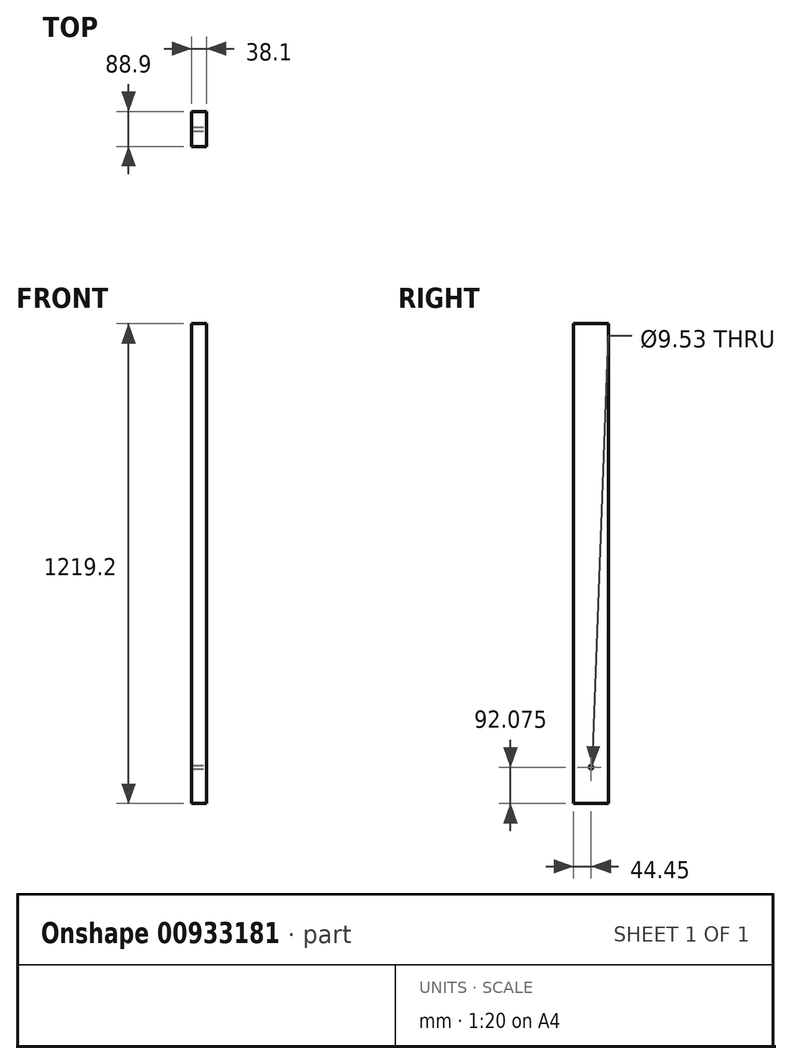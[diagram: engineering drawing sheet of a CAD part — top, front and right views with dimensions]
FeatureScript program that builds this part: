
annotation { "Feature Type Name" : "Feature", "Feature Type Description" : "" }
export const myFeature = defineFeature(function(context is Context, id is Id, definition is map)
    precondition{}
    {
        {
            var Q0;
            Q0=qCreatedBy(makeId("Top.planeOp"),FACE);
            var sketch = newSketch(context, id + "F0", { "sketchPlane" : qUnion([Q0])});
            skLineSegment(sketch, "E0.bottom", {"start": v(19.05, 44.45) * mm, "end": v(-19.05, 44.45) * mm});
            skLineSegment(sketch, "E0.top", {"start": v(19.05, -44.45) * mm, "end": v(-19.05, -44.45) * mm});
            skLineSegment(sketch, "E0.left", {"start": v(19.05, 44.45) * mm, "end": v(19.05, -44.45) * mm});
            skLineSegment(sketch, "E0.right", {"start": v(-19.05, 44.45) * mm, "end": v(-19.05, -44.45) * mm});
            skPoint(sketch, "E0.middle", {"position": v(0, 0) * mm});
            skSolve(sketch);
        }
        {
            var Q0;
            Q0 = qSketchRegion(id + "F0", true);
            extrude(context, id + "F1", {"entities" : qUnion([Q0]), "oppositeDirection" : true, "depth" : 1219.2 * mm, "offsetDistance" : 25.4 * mm});
        }
        {
            var Q0;
            Q0=makeQuery(id+"F1.opExtrude","SWEPT_FACE",FACE,{"disambiguationData":[OSD([sQuery(id+"F0.wireOp",EDGE,"E0.left")])]});
            var sketch = newSketch(context, id + "F2", { "sketchPlane" : qUnion([Q0])});
            skPoint(sketch, "E1", {"position": v(0, -1127.13) * mm});
            skSolve(sketch);
        }
        {
            var Q0;
            Q0=sQuery(id+"F2.wireOp",VERTEX,"E1");
            var Q1;
            Q1=makeQuery(id+"F1.opExtrude","SWEPT_BODY",BODY,{"disambiguationData":[OSD([sQuery(id+"F0.wireOp",EDGE,"E0.bottom"),sQuery(id+"F0.wireOp",EDGE,"E0.top"),sQuery(id+"F0.wireOp",EDGE,"E0.left"),sQuery(id+"F0.wireOp",EDGE,"E0.right")])]});
            hole(context, id + "F3", {"style" : HoleStyle.SIMPLE, "endStyle" : HoleEndStyle.THROUGH, "holeDiameter" : 9.52 * mm, "majorDiameter" : 6.35 * mm, "isTappedThrough" : true, "tappedDepth" : 12.7 * mm, "tapClearance" : 3, "locations" : qUnion([Q0]), "scope" : qUnion([Q1])});
        }
    });
